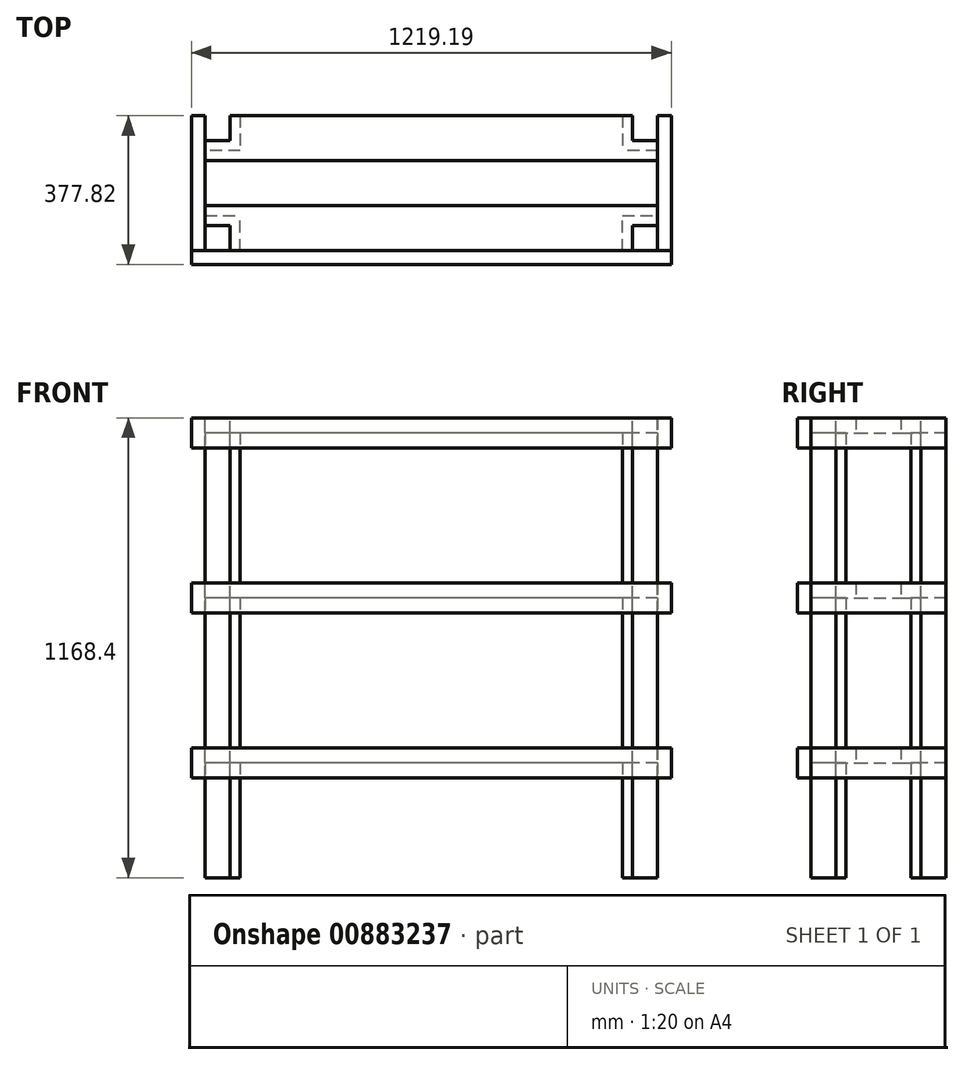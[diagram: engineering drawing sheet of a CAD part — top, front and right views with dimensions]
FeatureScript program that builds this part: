
annotation { "Feature Type Name" : "Feature", "Feature Type Description" : "" }
export const myFeature = defineFeature(function(context is Context, id is Id, definition is map)
    precondition{}
    {
        {
            var Q0;
            Q0=qCreatedBy(makeId("Top.planeOp"),FACE);
            var sketch = newSketch(context, id + "F0", { "sketchPlane" : qUnion([Q0])});
            skLineSegment(sketch, "E0.bottom", {"start": v(0, 0) * mm, "end": v(88.9, 0) * mm});
            skLineSegment(sketch, "E0.top", {"start": v(0, 88.9) * mm, "end": v(88.9, 88.9) * mm});
            skLineSegment(sketch, "E0.left", {"start": v(0, 0) * mm, "end": v(0, 88.9) * mm});
            skLineSegment(sketch, "E0.right", {"start": v(88.9, 0) * mm, "end": v(88.9, 88.9) * mm});
            skLineSegment(sketch, "E1.bottom", {"start": v(1060.45, 0) * mm, "end": v(1149.35, 0) * mm});
            skLineSegment(sketch, "E1.top", {"start": v(1060.45, 88.9) * mm, "end": v(1149.35, 88.9) * mm});
            skLineSegment(sketch, "E1.left", {"start": v(1060.45, 0) * mm, "end": v(1060.45, 88.9) * mm});
            skLineSegment(sketch, "E1.right", {"start": v(1149.35, 0) * mm, "end": v(1149.35, 88.9) * mm});
            skLineSegment(sketch, "E2.bottom", {"start": v(0, 254) * mm, "end": v(88.9, 254) * mm});
            skLineSegment(sketch, "E2.top", {"start": v(0, 342.9) * mm, "end": v(88.9, 342.9) * mm});
            skLineSegment(sketch, "E2.left", {"start": v(0, 254) * mm, "end": v(0, 342.9) * mm});
            skLineSegment(sketch, "E2.right", {"start": v(88.9, 254) * mm, "end": v(88.9, 342.9) * mm});
            skLineSegment(sketch, "E3.bottom", {"start": v(1060.45, 254) * mm, "end": v(1149.35, 254) * mm});
            skLineSegment(sketch, "E3.top", {"start": v(1060.45, 342.9) * mm, "end": v(1149.35, 342.9) * mm});
            skLineSegment(sketch, "E3.left", {"start": v(1060.45, 254) * mm, "end": v(1060.45, 342.9) * mm});
            skLineSegment(sketch, "E3.right", {"start": v(1149.35, 254) * mm, "end": v(1149.35, 342.9) * mm});
            skSolve(sketch);
        }
        {
            var Q0;
            Q0=qSketchRegion(id+"F0",true);
            extrude(context, id + "F1", {"entities" : qUnion([Q0]), "depth" : 1168.4 * mm, "offsetDistance" : 25.4 * mm});
        }
        {
            var Q0;
            Q0=makeQuery(id+"F1.opExtrude","SWEPT_FACE",FACE,{"disambiguationData":[OSD([sQuery(id+"F0.wireOp",EDGE,"E2.left")])]});
            var sketch = newSketch(context, id + "F2", { "sketchPlane" : qUnion([Q0])});
            skLineSegment(sketch, "E4.bottom", {"start": v(-342.9, 292.1) * mm, "end": v(-228.6, 292.1) * mm});
            skLineSegment(sketch, "E4.top", {"start": v(-342.9, 330.2) * mm, "end": v(-228.6, 330.2) * mm});
            skLineSegment(sketch, "E4.left", {"start": v(-342.9, 292.1) * mm, "end": v(-342.9, 330.2) * mm});
            skLineSegment(sketch, "E4.right", {"start": v(-228.6, 292.1) * mm, "end": v(-228.6, 330.2) * mm});
            skLineSegment(sketch, "E5.bottom", {"start": v(-228.6, 292.1) * mm, "end": v(-114.3, 292.1) * mm});
            skLineSegment(sketch, "E5.top", {"start": v(-228.6, 330.2) * mm, "end": v(-114.3, 330.2) * mm});
            skLineSegment(sketch, "E5.right", {"start": v(-114.3, 292.1) * mm, "end": v(-114.3, 330.2) * mm});
            skLineSegment(sketch, "E6.bottom", {"start": v(-114.3, 292.1) * mm, "end": v(0, 292.1) * mm});
            skLineSegment(sketch, "E6.top", {"start": v(-114.3, 330.2) * mm, "end": v(0, 330.2) * mm});
            skLineSegment(sketch, "E6.right", {"start": v(0, 292.1) * mm, "end": v(0, 330.2) * mm});
            skLineSegment(sketch, "E7.bottom", {"start": v(-342.9, 711.2) * mm, "end": v(-228.6, 711.2) * mm});
            skLineSegment(sketch, "E7.top", {"start": v(-342.9, 749.3) * mm, "end": v(-228.6, 749.3) * mm});
            skLineSegment(sketch, "E7.left", {"start": v(-342.9, 711.2) * mm, "end": v(-342.9, 749.3) * mm});
            skLineSegment(sketch, "E7.right", {"start": v(-228.6, 711.2) * mm, "end": v(-228.6, 749.3) * mm});
            skLineSegment(sketch, "E8.bottom", {"start": v(-228.6, 711.2) * mm, "end": v(-114.3, 711.2) * mm});
            skLineSegment(sketch, "E8.top", {"start": v(-228.6, 749.3) * mm, "end": v(-114.3, 749.3) * mm});
            skLineSegment(sketch, "E8.right", {"start": v(-114.3, 711.2) * mm, "end": v(-114.3, 749.3) * mm});
            skLineSegment(sketch, "E9.bottom", {"start": v(-114.3, 711.2) * mm, "end": v(0, 711.2) * mm});
            skLineSegment(sketch, "E9.top", {"start": v(-114.3, 749.3) * mm, "end": v(0, 749.3) * mm});
            skLineSegment(sketch, "E9.right", {"start": v(0, 711.2) * mm, "end": v(0, 749.3) * mm});
            skLineSegment(sketch, "E10.bottom", {"start": v(-342.9, 1130.3) * mm, "end": v(-228.6, 1130.3) * mm});
            skLineSegment(sketch, "E10.top", {"start": v(-342.9, 1168.4) * mm, "end": v(-228.6, 1168.4) * mm});
            skLineSegment(sketch, "E10.left", {"start": v(-342.9, 1130.3) * mm, "end": v(-342.9, 1168.4) * mm});
            skLineSegment(sketch, "E10.right", {"start": v(-228.6, 1130.3) * mm, "end": v(-228.6, 1168.4) * mm});
            skLineSegment(sketch, "E11.bottom", {"start": v(-228.6, 1130.3) * mm, "end": v(-114.3, 1130.3) * mm});
            skLineSegment(sketch, "E11.top", {"start": v(-228.6, 1168.4) * mm, "end": v(-114.3, 1168.4) * mm});
            skLineSegment(sketch, "E11.right", {"start": v(-114.3, 1130.3) * mm, "end": v(-114.3, 1168.4) * mm});
            skLineSegment(sketch, "E12.bottom", {"start": v(-114.3, 1130.3) * mm, "end": v(0, 1130.3) * mm});
            skLineSegment(sketch, "E12.top", {"start": v(-114.3, 1168.4) * mm, "end": v(0, 1168.4) * mm});
            skLineSegment(sketch, "E12.right", {"start": v(0, 1130.3) * mm, "end": v(0, 1168.4) * mm});
            skLineSegment(sketch, "E13", {"start": v(0, 711.2) * mm, "end": v(0, 330.2) * mm, "construction": true});
            skLineSegment(sketch, "E14", {"start": v(0, 749.3) * mm, "end": v(0, 1130.3) * mm, "construction": true});
            skLineSegment(sketch, "E15.bottom", {"start": v(0, 749.3) * mm, "end": v(34.92, 749.3) * mm, "construction": true});
            skLineSegment(sketch, "E15.top", {"start": v(0, 673.1) * mm, "end": v(34.92, 673.1) * mm, "construction": true});
            skLineSegment(sketch, "E15.left", {"start": v(0, 749.3) * mm, "end": v(0, 673.1) * mm, "construction": true});
            skLineSegment(sketch, "E15.right", {"start": v(34.92, 749.3) * mm, "end": v(34.92, 673.1) * mm, "construction": true});
            skSolve(sketch);
        }
        {
            var Q0;
            {var subQ0=sQuery(id+"F2.wireOp",EDGE,"E10.right");Q0=makeQuery(id+"F2.imprint","IMPRINT",FACE,{"disambiguationData":[TD([[makeQuery(id+"F2.imprint","IMPRINT",EDGE,{"derivedFrom":subQ0}),1.0]])]});}
            var Q1;
            {var subQ0=sQuery(id+"F2.wireOp",EDGE,"E10.left");Q1=makeQuery(id+"F2.imprint","IMPRINT",FACE,{"disambiguationData":[TD([[makeQuery(id+"F2.imprint","IMPRINT",EDGE,{"derivedFrom":subQ0}),1.0]])]});}
            var Q2;
            Q2=makeQuery(id+"F2.imprint","IMPRINT",FACE,{"disambiguationData":[TD([[makeQuery(id+"F2.imprint","IMPRINT",EDGE,{"derivedFrom":sQuery(id+"F2.wireOp",EDGE,"E12.bottom")}),1.0]])]});
            var Q3;
            {var subQ0=sQuery(id+"F2.wireOp",EDGE,"E7.left");Q3=makeQuery(id+"F2.imprint","IMPRINT",FACE,{"disambiguationData":[TD([[makeQuery(id+"F2.imprint","IMPRINT",EDGE,{"derivedFrom":subQ0}),1.0]])]});}
            var Q4;
            {var subQ0=sQuery(id+"F2.wireOp",EDGE,"E7.right");Q4=makeQuery(id+"F2.imprint","IMPRINT",FACE,{"disambiguationData":[TD([[makeQuery(id+"F2.imprint","IMPRINT",EDGE,{"derivedFrom":subQ0}),1.0]])]});}
            var Q5;
            {var subQ0=sQuery(id+"F2.wireOp",EDGE,"E4.left");Q5=makeQuery(id+"F2.imprint","IMPRINT",FACE,{"disambiguationData":[TD([[makeQuery(id+"F2.imprint","IMPRINT",EDGE,{"derivedFrom":subQ0}),1.0]])]});}
            var Q6;
            {var subQ0=sQuery(id+"F2.wireOp",EDGE,"E4.right");Q6=makeQuery(id+"F2.imprint","IMPRINT",FACE,{"disambiguationData":[TD([[makeQuery(id+"F2.imprint","IMPRINT",EDGE,{"derivedFrom":subQ0}),1.0]])]});}
            var Q7;
            Q7=makeQuery(id+"F2.imprint","IMPRINT",FACE,{"disambiguationData":[TD([[makeQuery(id+"F2.imprint","IMPRINT",EDGE,{"derivedFrom":sQuery(id+"F2.wireOp",EDGE,"E6.bottom")}),1.0]])]});
            var Q8;
            Q8=makeQuery(id+"F2.imprint","IMPRINT",FACE,{"disambiguationData":[TD([[makeQuery(id+"F2.imprint","IMPRINT",EDGE,{"derivedFrom":sQuery(id+"F2.wireOp",EDGE,"E9.bottom")}),1.0]])]});
            var Q9;
            Q9=makeQuery(id+"F1.opExtrude","SWEPT_FACE",FACE,{"disambiguationData":[OSD([sQuery(id+"F0.wireOp",EDGE,"E1.right")])]});
            extrude(context, id + "F3", {"entities" : qUnion([Q0, Q1, Q2, Q3, Q4, Q5, Q6, Q7, Q8]), "endBound" : BoundingType.UP_TO_SURFACE, "oppositeDirection" : true, "depth" : 25.4 * mm, "endBoundEntityFace" : qUnion([Q9]), "offsetDistance" : 25.4 * mm});
        }
        {
            var Q0;
            Q0=makeQuery(id+"F2.imprint","IMPRINT",FACE,{"disambiguationData":[TD([[makeQuery(id+"F2.imprint","IMPRINT",EDGE,{"derivedFrom":sQuery(id+"F2.wireOp",EDGE,"E11.bottom")}),1.0]])]});
            var Q1;
            Q1=makeQuery(id+"F2.imprint","IMPRINT",FACE,{"disambiguationData":[TD([[makeQuery(id+"F2.imprint","IMPRINT",EDGE,{"derivedFrom":sQuery(id+"F2.wireOp",EDGE,"E8.bottom")}),1.0]])]});
            var Q2;
            Q2=makeQuery(id+"F2.imprint","IMPRINT",FACE,{"disambiguationData":[TD([[makeQuery(id+"F2.imprint","IMPRINT",EDGE,{"derivedFrom":sQuery(id+"F2.wireOp",EDGE,"E5.bottom")}),1.0]])]});
            var Q3;
            Q3=makeQuery(id+"F3.opExtrude","CAP_FACE",FACE,{"disambiguationData":[OSD([sQuery(id+"F2.wireOp",EDGE,"E7.bottom"),sQuery(id+"F2.wireOp",EDGE,"E7.top"),sQuery(id+"F2.wireOp",EDGE,"E7.left"),sQuery(id+"F2.wireOp",EDGE,"E7.right")])],"isStart":false});
            extrude(context, id + "F4", {"entities" : qUnion([Q0, Q1, Q2]), "endBound" : BoundingType.UP_TO_SURFACE, "oppositeDirection" : true, "depth" : 25.4 * mm, "endBoundEntityFace" : qUnion([Q3]), "offsetDistance" : 25.4 * mm});
        }
        {
            var Q0;
            Q0=makeQuery(id+"F3.opExtrude","SWEPT_FACE",FACE,{"disambiguationData":[OSD([sQuery(id+"F2.wireOp",EDGE,"E12.top")])]});
            var sketch = newSketch(context, id + "F5", { "sketchPlane" : qUnion([Q0])});
            skLineSegment(sketch, "E16.bottom", {"start": v(0, 0) * mm, "end": v(63.5, 0) * mm});
            skLineSegment(sketch, "E16.top", {"start": v(0, 63.5) * mm, "end": v(63.5, 63.5) * mm});
            skLineSegment(sketch, "E16.left", {"start": v(0, 0) * mm, "end": v(0, 63.5) * mm});
            skLineSegment(sketch, "E16.right", {"start": v(63.5, 0) * mm, "end": v(63.5, 63.5) * mm});
            skLineSegment(sketch, "E17.bottom", {"start": v(1085.85, 0) * mm, "end": v(1149.35, 0) * mm});
            skLineSegment(sketch, "E17.top", {"start": v(1085.85, 63.5) * mm, "end": v(1149.35, 63.5) * mm});
            skLineSegment(sketch, "E17.left", {"start": v(1085.85, 0) * mm, "end": v(1085.85, 63.5) * mm});
            skLineSegment(sketch, "E17.right", {"start": v(1149.35, 0) * mm, "end": v(1149.35, 63.5) * mm});
            skLineSegment(sketch, "E18.bottom", {"start": v(1085.85, 279.4) * mm, "end": v(1149.35, 279.4) * mm});
            skLineSegment(sketch, "E18.top", {"start": v(1085.85, 342.9) * mm, "end": v(1149.35, 342.9) * mm});
            skLineSegment(sketch, "E18.left", {"start": v(1085.85, 279.4) * mm, "end": v(1085.85, 342.9) * mm});
            skLineSegment(sketch, "E18.right", {"start": v(1149.35, 279.4) * mm, "end": v(1149.35, 342.9) * mm});
            skLineSegment(sketch, "E19.bottom", {"start": v(0, 279.4) * mm, "end": v(63.5, 279.4) * mm});
            skLineSegment(sketch, "E19.top", {"start": v(0, 342.9) * mm, "end": v(63.5, 342.9) * mm});
            skLineSegment(sketch, "E19.left", {"start": v(0, 279.4) * mm, "end": v(0, 342.9) * mm});
            skLineSegment(sketch, "E19.right", {"start": v(63.5, 279.4) * mm, "end": v(63.5, 342.9) * mm});
            skSolve(sketch);
        }
        {
            var Q0;
            Q0=qSketchRegion(id+"F5",true);
            extrude(context, id + "F6", {"entities" : qUnion([Q0]), "operationType" : NewBodyOperationType.REMOVE, "endBound" : BoundingType.THROUGH_ALL, "oppositeDirection" : true, "depth" : 25.4 * mm, "offsetDistance" : 25.4 * mm});
        }
        {
            var Q0;
            Q0=makeQuery(id+"F3.opExtrude","SWEPT_BODY",BODY,{"disambiguationData":[OSD([sQuery(id+"F2.wireOp",EDGE,"E7.bottom"),sQuery(id+"F2.wireOp",EDGE,"E7.top"),sQuery(id+"F2.wireOp",EDGE,"E7.left"),sQuery(id+"F2.wireOp",EDGE,"E7.right")])]});
            var Q1;
            Q1=makeQuery(id+"F3.opExtrude","SWEPT_BODY",BODY,{"disambiguationData":[OSD([sQuery(id+"F2.wireOp",EDGE,"E9.bottom"),sQuery(id+"F2.wireOp",EDGE,"E9.top"),sQuery(id+"F2.wireOp",EDGE,"E8.right"),sQuery(id+"F2.wireOp",EDGE,"E9.right")])]});
            var Q2;
            Q2=makeQuery(id+"F3.opExtrude","SWEPT_BODY",BODY,{"disambiguationData":[OSD([sQuery(id+"F2.wireOp",EDGE,"E4.bottom"),sQuery(id+"F2.wireOp",EDGE,"E4.top"),sQuery(id+"F2.wireOp",EDGE,"E4.left"),sQuery(id+"F2.wireOp",EDGE,"E4.right")])]});
            var Q3;
            Q3=makeQuery(id+"F3.opExtrude","SWEPT_BODY",BODY,{"disambiguationData":[OSD([sQuery(id+"F2.wireOp",EDGE,"E6.bottom"),sQuery(id+"F2.wireOp",EDGE,"E6.top"),sQuery(id+"F2.wireOp",EDGE,"E5.right"),sQuery(id+"F2.wireOp",EDGE,"E6.right")])]});
            var Q4;
            Q4=makeQuery(id+"F3.opExtrude","SWEPT_BODY",BODY,{"disambiguationData":[OSD([sQuery(id+"F2.wireOp",EDGE,"E10.bottom"),sQuery(id+"F2.wireOp",EDGE,"E10.top"),sQuery(id+"F2.wireOp",EDGE,"E10.left"),sQuery(id+"F2.wireOp",EDGE,"E10.right")])]});
            var Q5;
            Q5=makeQuery(id+"F3.opExtrude","SWEPT_BODY",BODY,{"disambiguationData":[OSD([sQuery(id+"F2.wireOp",EDGE,"E12.bottom"),sQuery(id+"F2.wireOp",EDGE,"E12.top"),sQuery(id+"F2.wireOp",EDGE,"E11.right"),sQuery(id+"F2.wireOp",EDGE,"E12.right")])]});
            var Q6;
            Q6=makeQuery(id+"F1.opExtrude","SWEPT_BODY",BODY,{"disambiguationData":[OSD([sQuery(id+"F0.wireOp",EDGE,"E2.bottom"),sQuery(id+"F0.wireOp",EDGE,"E2.top"),sQuery(id+"F0.wireOp",EDGE,"E2.left"),sQuery(id+"F0.wireOp",EDGE,"E2.right")])]});
            var Q7;
            Q7=makeQuery(id+"F1.opExtrude","SWEPT_BODY",BODY,{"disambiguationData":[OSD([sQuery(id+"F0.wireOp",EDGE,"E0.bottom"),sQuery(id+"F0.wireOp",EDGE,"E0.top"),sQuery(id+"F0.wireOp",EDGE,"E0.left"),sQuery(id+"F0.wireOp",EDGE,"E0.right")])]});
            var Q8;
            Q8=makeQuery(id+"F1.opExtrude","SWEPT_BODY",BODY,{"disambiguationData":[OSD([sQuery(id+"F0.wireOp",EDGE,"E3.bottom"),sQuery(id+"F0.wireOp",EDGE,"E3.top"),sQuery(id+"F0.wireOp",EDGE,"E3.left"),sQuery(id+"F0.wireOp",EDGE,"E3.right")])]});
            var Q9;
            Q9=makeQuery(id+"F1.opExtrude","SWEPT_BODY",BODY,{"disambiguationData":[OSD([sQuery(id+"F0.wireOp",EDGE,"E1.bottom"),sQuery(id+"F0.wireOp",EDGE,"E1.top"),sQuery(id+"F0.wireOp",EDGE,"E1.left"),sQuery(id+"F0.wireOp",EDGE,"E1.right")])]});
            booleanBodies(context, id + "F7", {"operationType" : BooleanOperationType.SUBTRACTION, "tools" : qUnion([Q0, Q1, Q2, Q3, Q4, Q5]), "targets" : qUnion([Q6, Q7, Q8, Q9]), "keepTools" : true});
        }
        {
            var Q0;
            Q0=makeQuery(id+"F1.opExtrude","SWEPT_FACE",FACE,{"disambiguationData":[OSD([sQuery(id+"F0.wireOp",EDGE,"E3.top")])]});
            var sketch = newSketch(context, id + "F8", { "sketchPlane" : qUnion([Q0])});
            skLineSegment(sketch, "E20.bottom", {"start": v(-1149.35, 1168.4) * mm, "end": v(-1184.28, 1168.4) * mm});
            skLineSegment(sketch, "E20.top", {"start": v(-1149.35, 1092.2) * mm, "end": v(-1184.28, 1092.2) * mm});
            skLineSegment(sketch, "E20.left", {"start": v(-1149.35, 1168.4) * mm, "end": v(-1149.35, 1092.2) * mm});
            skLineSegment(sketch, "E20.right", {"start": v(-1184.28, 1168.4) * mm, "end": v(-1184.28, 1092.2) * mm});
            skLineSegment(sketch, "E21.bottom", {"start": v(-1149.35, 749.3) * mm, "end": v(-1184.28, 749.3) * mm});
            skLineSegment(sketch, "E21.top", {"start": v(-1149.35, 673.1) * mm, "end": v(-1184.28, 673.1) * mm});
            skLineSegment(sketch, "E21.left", {"start": v(-1149.35, 749.3) * mm, "end": v(-1149.35, 673.1) * mm});
            skLineSegment(sketch, "E21.right", {"start": v(-1184.28, 749.3) * mm, "end": v(-1184.28, 673.1) * mm});
            skLineSegment(sketch, "E22.bottom", {"start": v(-1149.35, 330.2) * mm, "end": v(-1184.28, 330.2) * mm});
            skLineSegment(sketch, "E22.top", {"start": v(-1149.35, 254) * mm, "end": v(-1184.28, 254) * mm});
            skLineSegment(sketch, "E22.left", {"start": v(-1149.35, 330.2) * mm, "end": v(-1149.35, 254) * mm});
            skLineSegment(sketch, "E22.right", {"start": v(-1184.28, 330.2) * mm, "end": v(-1184.28, 254) * mm});
            skLineSegment(sketch, "E23.bottom", {"start": v(0, 1168.4) * mm, "end": v(34.93, 1168.4) * mm});
            skLineSegment(sketch, "E23.top", {"start": v(0, 1092.2) * mm, "end": v(34.93, 1092.2) * mm});
            skLineSegment(sketch, "E23.left", {"start": v(0, 1168.4) * mm, "end": v(0, 1092.2) * mm});
            skLineSegment(sketch, "E23.right", {"start": v(34.93, 1168.4) * mm, "end": v(34.93, 1092.2) * mm});
            skLineSegment(sketch, "E24.bottom", {"start": v(0, 749.3) * mm, "end": v(34.93, 749.3) * mm});
            skLineSegment(sketch, "E24.top", {"start": v(0, 673.1) * mm, "end": v(34.93, 673.1) * mm});
            skLineSegment(sketch, "E24.left", {"start": v(0, 749.3) * mm, "end": v(0, 673.1) * mm});
            skLineSegment(sketch, "E24.right", {"start": v(34.93, 749.3) * mm, "end": v(34.93, 673.1) * mm});
            skLineSegment(sketch, "E25.bottom", {"start": v(0, 330.2) * mm, "end": v(34.93, 330.2) * mm});
            skLineSegment(sketch, "E25.top", {"start": v(0, 254) * mm, "end": v(34.93, 254) * mm});
            skLineSegment(sketch, "E25.left", {"start": v(0, 330.2) * mm, "end": v(0, 254) * mm});
            skLineSegment(sketch, "E25.right", {"start": v(34.93, 330.2) * mm, "end": v(34.93, 254) * mm});
            skSolve(sketch);
        }
        {
            var Q0;
            Q0=qSketchRegion(id+"F8",true);
            var Q1;
            Q1=makeQuery(id+"F1.opExtrude","SWEPT_FACE",FACE,{"disambiguationData":[OSD([sQuery(id+"F0.wireOp",EDGE,"E0.bottom")])]});
            extrude(context, id + "F9", {"entities" : qUnion([Q0]), "endBound" : BoundingType.UP_TO_SURFACE, "oppositeDirection" : true, "depth" : 25.4 * mm, "endBoundEntityFace" : qUnion([Q1]), "offsetDistance" : 25.4 * mm});
        }
        {
            var Q0;
            Q0=makeQuery(id+"F1.opExtrude","SWEPT_FACE",FACE,{"disambiguationData":[OSD([sQuery(id+"F0.wireOp",EDGE,"E0.bottom")])]});
            var sketch = newSketch(context, id + "F10", { "sketchPlane" : qUnion([Q0])});
            skLineSegment(sketch, "E26.bottom", {"start": v(-34.93, 330.2) * mm, "end": v(1184.28, 330.2) * mm});
            skLineSegment(sketch, "E26.top", {"start": v(-34.93, 254) * mm, "end": v(1184.28, 254) * mm});
            skLineSegment(sketch, "E26.left", {"start": v(-34.93, 330.2) * mm, "end": v(-34.93, 254) * mm});
            skLineSegment(sketch, "E26.right", {"start": v(1184.28, 330.2) * mm, "end": v(1184.28, 254) * mm});
            skLineSegment(sketch, "E27.bottom", {"start": v(-34.93, 749.3) * mm, "end": v(1184.28, 749.3) * mm});
            skLineSegment(sketch, "E27.top", {"start": v(-34.93, 673.1) * mm, "end": v(1184.28, 673.1) * mm});
            skLineSegment(sketch, "E27.left", {"start": v(-34.93, 749.3) * mm, "end": v(-34.93, 673.1) * mm});
            skLineSegment(sketch, "E27.right", {"start": v(1184.28, 749.3) * mm, "end": v(1184.28, 673.1) * mm});
            skLineSegment(sketch, "E28.bottom", {"start": v(-34.93, 1168.4) * mm, "end": v(1184.28, 1168.4) * mm});
            skLineSegment(sketch, "E28.top", {"start": v(-34.93, 1092.2) * mm, "end": v(1184.28, 1092.2) * mm});
            skLineSegment(sketch, "E28.left", {"start": v(-34.93, 1168.4) * mm, "end": v(-34.93, 1092.2) * mm});
            skLineSegment(sketch, "E28.right", {"start": v(1184.28, 1168.4) * mm, "end": v(1184.28, 1092.2) * mm});
            skSolve(sketch);
        }
        {
            var Q0;
            Q0=qSketchRegion(id+"F10",true);
            extrude(context, id + "F11", {"entities" : qUnion([Q0]), "depth" : 34.92 * mm, "offsetDistance" : 25.4 * mm});
        }
    });
